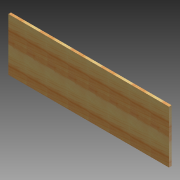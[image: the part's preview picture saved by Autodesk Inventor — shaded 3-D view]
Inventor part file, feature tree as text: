
AUTODESK INVENTOR PART (.ipt)
format: ipt  version: 2012 (Build 160160000, 160)  size: 84,992 bytes
history: native  units: in
note: dims shown in document units (in); Inventor stores cm internally (conversion verified against a paired STEP export)
features: extrude x1, sketch x1
ambient origin geometry x8: Origin, YZ Plane, XZ Plane, XY Plane, X Axis, Y Axis, Z Axis, Center Point
bodies: Solid1 (feature_tree)
feature tree (2):
  extrude  "Extrusion1"  Depth=9.0in
  sketch  "Sketch1"  dims[d0=27.4375in d1=9.0in d2=0.4375in d3=0.0in]
